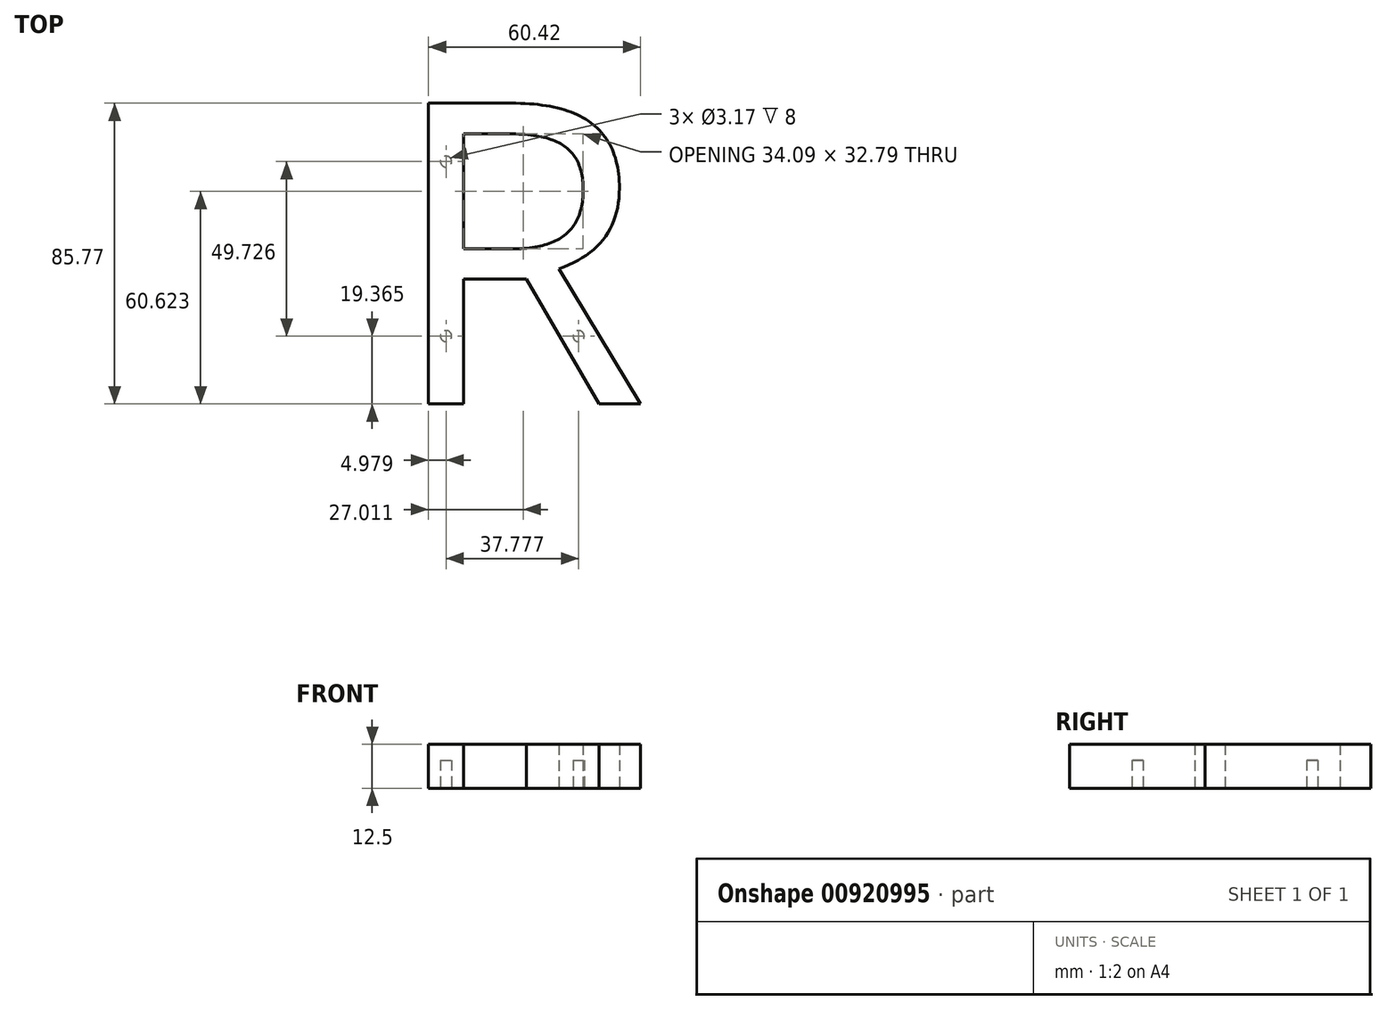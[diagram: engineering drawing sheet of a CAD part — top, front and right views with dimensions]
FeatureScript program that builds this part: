
annotation { "Feature Type Name" : "Feature", "Feature Type Description" : "" }
export const myFeature = defineFeature(function(context is Context, id is Id, definition is map)
    precondition{}
    {
        {
            var Q0;
            Q0=qCreatedBy(makeId("Top.planeOp"),FACE);
            var sketch = newSketch(context, id + "F0", { "sketchPlane" : qUnion([Q0])});
            skText(sketch, "E0", { "text": "R", "fontName": "OpenSans-Regular.ttf"});
            const initialGuessF0  = {"E0": [-0.03414, -0.04928, 1, 0, 0.0865]};
            skSetInitialGuess(sketch, initialGuessF0);
            skSolve(sketch);
        }
        {
            var Q0;
            Q0=makeQuery(id+"F0.imprint","IMPRINT",FACE,{"disambiguationData":[TD([[makeQuery(id+"F0.imprint","IMPRINT",EDGE,{"derivedFrom":sQuery(id+"F0.wireOp",EDGE,"E0.sketch_text.stroke-0")}),-1.0]])]});
            extrude(context, id + "F1", {"entities" : qUnion([Q0]), "depth" : 12.5 * mm, "offsetDistance" : 25 * mm});
        }
        {
            var Q0;
            Q0=makeQuery(id+"F1.opExtrude","CAP_FACE",FACE,{"disambiguationData":[OSD([sQuery(id+"F0.wireOp",EDGE,"E0.sketch_text.stroke-0"),sQuery(id+"F0.wireOp",EDGE,"E0.sketch_text.stroke-1"),sQuery(id+"F0.wireOp",EDGE,"E0.sketch_text.stroke-2"),sQuery(id+"F0.wireOp",EDGE,"E0.sketch_text.stroke-3"),sQuery(id+"F0.wireOp",EDGE,"E0.sketch_text.stroke-4"),sQuery(id+"F0.wireOp",EDGE,"E0.sketch_text.stroke-5"),sQuery(id+"F0.wireOp",EDGE,"E0.sketch_text.stroke-6"),sQuery(id+"F0.wireOp",EDGE,"E0.sketch_text.stroke-7"),sQuery(id+"F0.wireOp",EDGE,"E0.sketch_text.stroke-8"),sQuery(id+"F0.wireOp",EDGE,"E0.sketch_text.stroke-9"),sQuery(id+"F0.wireOp",EDGE,"E0.sketch_text.stroke-10"),sQuery(id+"F0.wireOp",EDGE,"E0.sketch_text.stroke-11"),sQuery(id+"F0.wireOp",EDGE,"E0.sketch_text.stroke-12"),sQuery(id+"F0.wireOp",EDGE,"E0.sketch_text.stroke-13"),sQuery(id+"F0.wireOp",EDGE,"E0.sketch_text.stroke-14"),sQuery(id+"F0.wireOp",EDGE,"E0.sketch_text.stroke-15"),sQuery(id+"F0.wireOp",EDGE,"E0.sketch_text.stroke-16"),sQuery(id+"F0.wireOp",EDGE,"E0.sketch_text.stroke-17")])],"isStart":true});
            var sketch = newSketch(context, id + "F2", { "sketchPlane" : qUnion([Q0])});
            skLineSegment(sketch, "E1", {"start": v(-17.37, 49.28) * mm, "end": v(-17.37, -36.48) * mm, "construction": true});
            skCircle(sketch, "E2", {"center": v(-17.37, 29.92) * mm, "radius": 1.59 * mm});
            skCircle(sketch, "E3", {"center": v(-17.37, -19.81) * mm, "radius": 1.59 * mm});
            skCircle(sketch, "E4", {"center": v(20.4, 29.92) * mm, "radius": 1.59 * mm});
            skSolve(sketch);
        }
        {
            var Q0;
            Q0=makeQuery(id+"F2.imprint","IMPRINT",FACE,{"disambiguationData":[TD([[makeQuery(id+"F2.imprint","IMPRINT",EDGE,{"derivedFrom":sQuery(id+"F2.wireOp",EDGE,"E2")}),1.0]])]});
            var Q1;
            Q1=makeQuery(id+"F2.imprint","IMPRINT",FACE,{"disambiguationData":[TD([[makeQuery(id+"F2.imprint","IMPRINT",EDGE,{"derivedFrom":sQuery(id+"F2.wireOp",EDGE,"E4")}),1.0]])]});
            var Q2;
            Q2=makeQuery(id+"F2.imprint","IMPRINT",FACE,{"disambiguationData":[TD([[makeQuery(id+"F2.imprint","IMPRINT",EDGE,{"derivedFrom":sQuery(id+"F2.wireOp",EDGE,"E3")}),1.0]])]});
            var Q3;
            Q3=sQuery(id+"F2.wireOp",EDGE,"E2");
            var Q4;
            Q4=sQuery(id+"F2.wireOp",EDGE,"E4");
            var Q5;
            Q5=sQuery(id+"F2.wireOp",EDGE,"E3");
            extrude(context, id + "F3", {"entities" : qUnion([Q0, Q1, Q2]), "operationType" : NewBodyOperationType.REMOVE, "surfaceEntities" : qUnion([Q3, Q4, Q5]), "oppositeDirection" : true, "depth" : 8 * mm, "offsetDistance" : 25 * mm});
        }
    });
